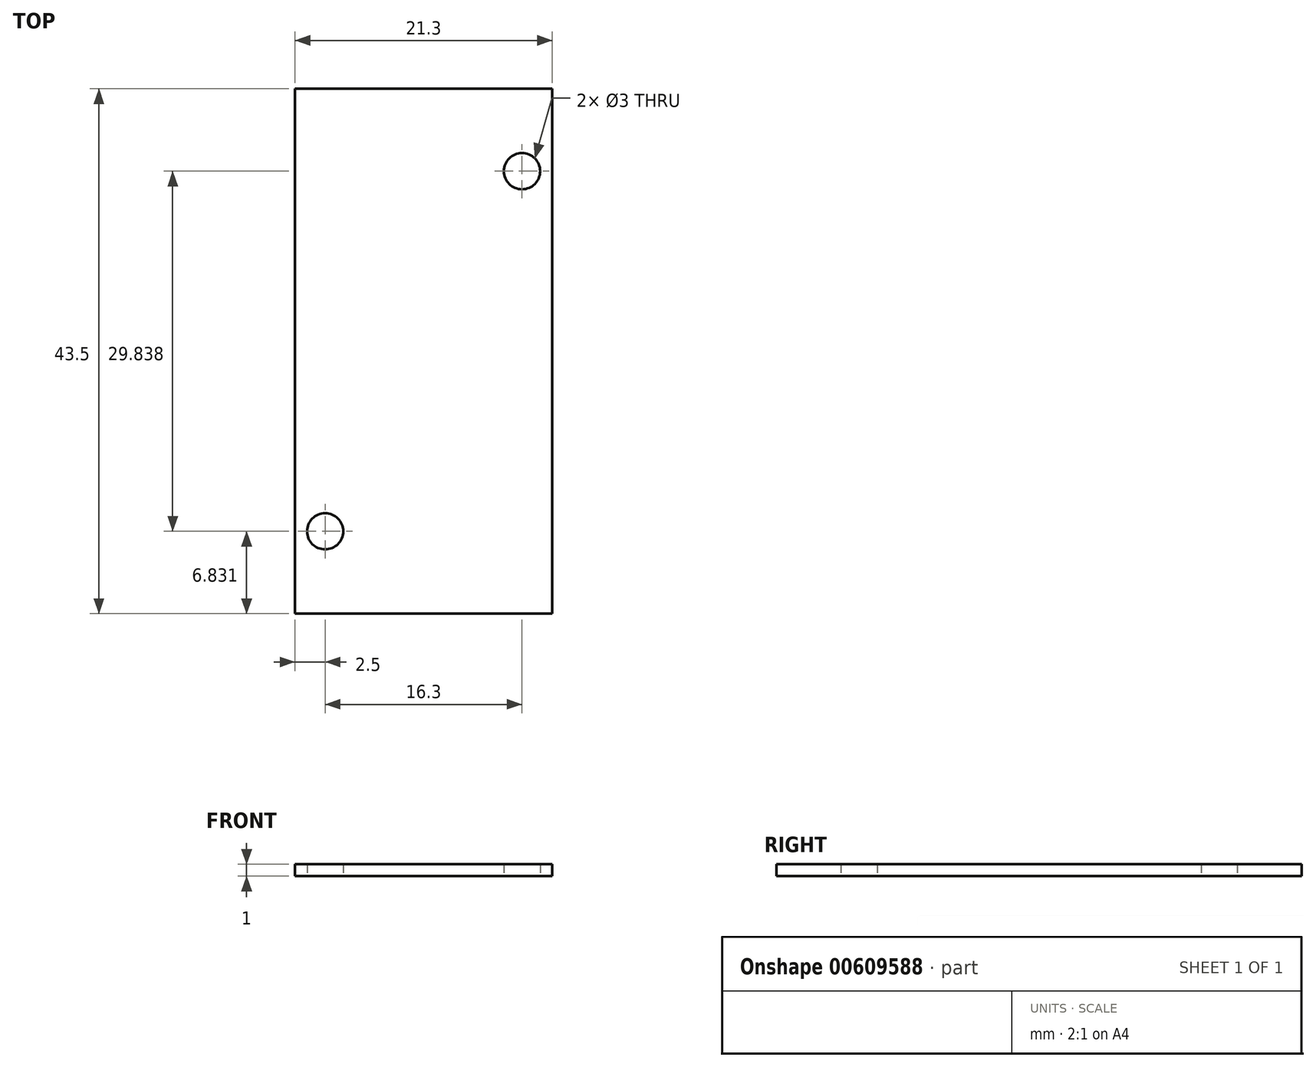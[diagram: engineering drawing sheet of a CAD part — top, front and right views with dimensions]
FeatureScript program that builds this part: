
annotation { "Feature Type Name" : "Feature", "Feature Type Description" : "" }
export const myFeature = defineFeature(function(context is Context, id is Id, definition is map)
    precondition{}
    {
        {
            var Q0;
            Q0=qCreatedBy(makeId("Top.planeOp"),FACE);
            var sketch = newSketch(context, id + "F0", { "sketchPlane" : qUnion([Q0])});
            skLineSegment(sketch, "E0.bottom", {"start": v(10.65, -21.75) * mm, "end": v(-10.65, -21.75) * mm});
            skLineSegment(sketch, "E0.top", {"start": v(10.65, 21.75) * mm, "end": v(-10.65, 21.75) * mm});
            skLineSegment(sketch, "E0.left", {"start": v(10.65, -21.75) * mm, "end": v(10.65, 21.75) * mm});
            skLineSegment(sketch, "E0.right", {"start": v(-10.65, -21.75) * mm, "end": v(-10.65, 21.75) * mm});
            skPoint(sketch, "E0.middle", {"position": v(0, 0) * mm});
            skCircle(sketch, "E1", {"center": v(-8.15, -14.92) * mm, "radius": 1.5 * mm});
            skCircle(sketch, "E2", {"center": v(8.15, 14.92) * mm, "radius": 1.5 * mm});
            skLineSegment(sketch, "E3", {"start": v(0, 0) * mm, "end": v(8.15, 14.92) * mm, "construction": true});
            skLineSegment(sketch, "E4", {"start": v(0, 0) * mm, "end": v(-8.15, -14.92) * mm, "construction": true});
            skLineSegment(sketch, "E5", {"start": v(-8.15, -14.92) * mm, "end": v(-10.65, -14.92) * mm, "construction": true});
            skLineSegment(sketch, "E6", {"start": v(8.15, 14.92) * mm, "end": v(10.65, 14.92) * mm, "construction": true});
            skSolve(sketch);
        }
        {
            var Q0;
            Q0 = qSketchRegion(id + "F0", true);
            extrude(context, id + "F1", {"entities" : qUnion([Q0]), "depth" : 1 * mm, "offsetDistance" : 25 * mm});
        }
    });
